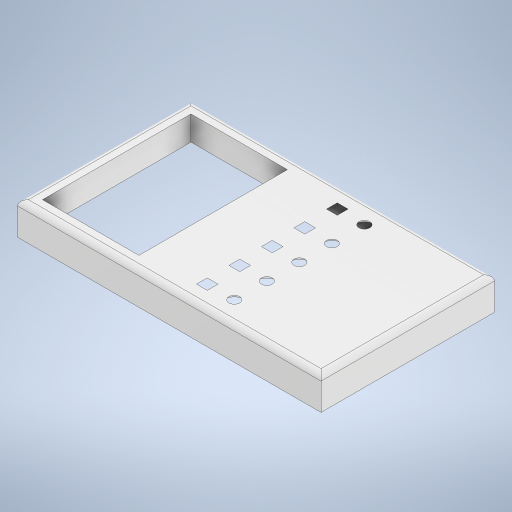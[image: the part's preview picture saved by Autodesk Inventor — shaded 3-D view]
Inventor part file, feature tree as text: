
AUTODESK INVENTOR PART (.ipt)
format: ipt  version: 2023 (Build 270158000, 158)  size: 357,888 bytes
history: native  units: in
note: dims shown in document units (in); Inventor stores cm internally (conversion verified against a paired STEP export)
features: delete_face x8, extrude x1, fillet x1, shell x1, sketch x1
ambient origin geometry x8: Origin, YZ Plane, XZ Plane, XY Plane, X Axis, Y Axis, Z Axis, Center Point
bodies: Solid1 (feature_tree)
feature tree (12):
  extrude  "Extrusion1"  Depth=4.0in
  fillet  "Fillet1"  Radius=2.225in
  shell  "Shell1"  Thickness=3.425in
  delete_face  "Delete Face1"
  delete_face  "Delete Face2"
  delete_face  "Delete Face3"
  delete_face  "Delete Face4"
  delete_face  "Delete Face5"
  delete_face  "Delete Face6"
  delete_face  "Delete Face7"
  delete_face  "Delete Face8"
  sketch  "Sketch1"  dims[d0=7.0in d1=4.0in d2=2.225in d3=3.425in d4=0.2875in d5=0.2875in d6=0.25in d7=0.25in d8=0.25in d9=0.25in d10=0.25in d13=0.25in d14=0.25in d15=0.25in d16=0.25in d17=0.375in d18=0.5in d19=0.25in d20=0.25in d21=0.25in d22=0.25in d23=0.25in d24=0.25in d25=0.5in d26=0.5in d27=0.5in d28=0.5in d29=0.75in d30=0.75in d31=0.75in d32=0.75in d33=3.0in d34=3.0in d35=3.0in d36=3.0in d37=3.0in d38=2.5in d39=2.5in d40=2.5in d41=2.5in d42=2.5in d43=0.75in d44=0.0in d45=0.125in d46=0.1in]
